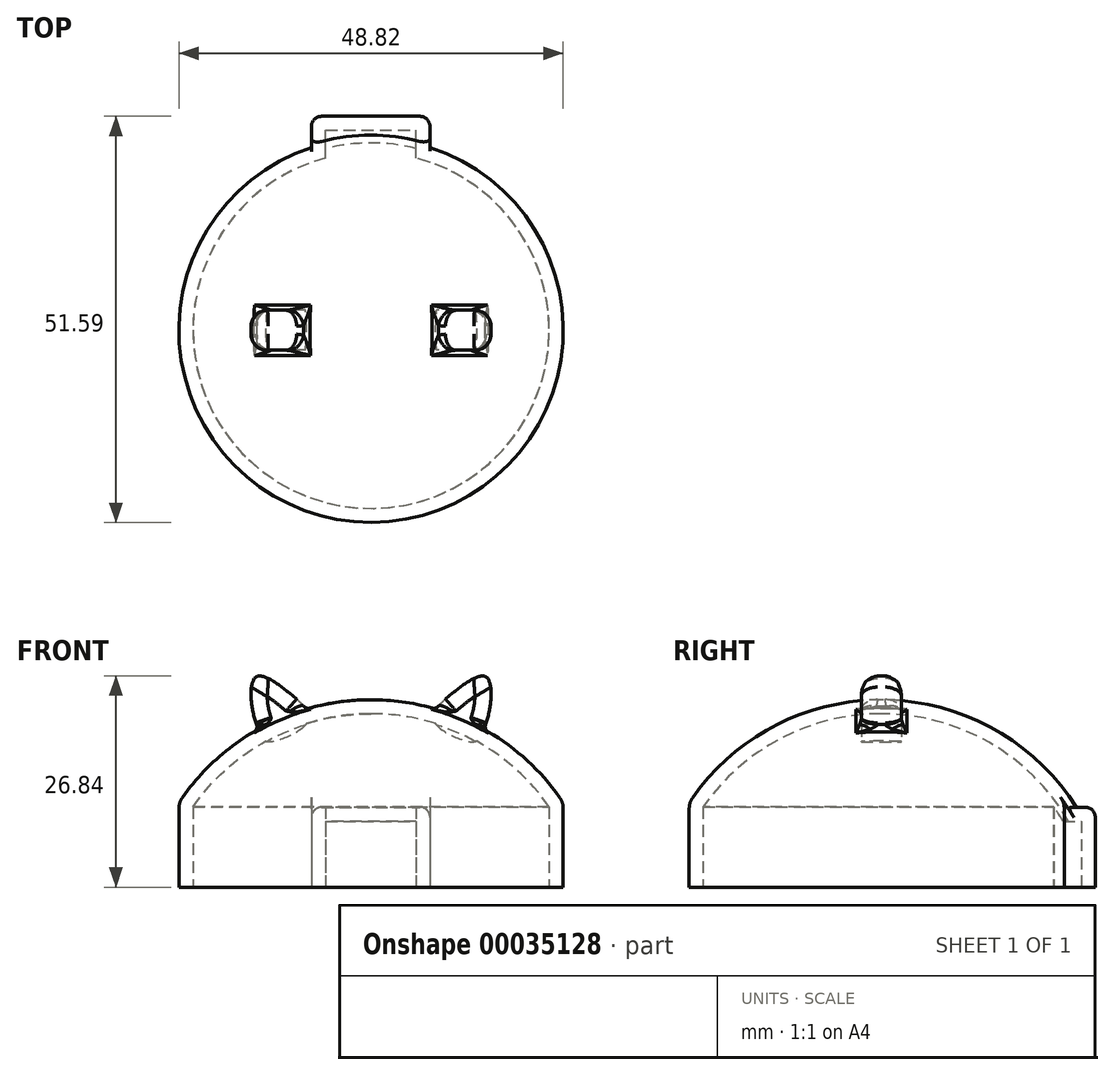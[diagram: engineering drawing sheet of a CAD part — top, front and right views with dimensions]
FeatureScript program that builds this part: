
annotation { "Feature Type Name" : "Feature", "Feature Type Description" : "" }
export const myFeature = defineFeature(function(context is Context, id is Id, definition is map)
    precondition{}
    {
        {
            var Q0;
            Q0=qCreatedBy(makeId("Top.planeOp"),FACE);
            var sketch = newSketch(context, id + "F0", { "sketchPlane" : qUnion([Q0])});
            skCircle(sketch, "E0", {"center": v(0, 0) * mm, "radius": 22.38 * mm});
            skLineSegment(sketch, "E1.bottom", {"start": v(-5.78, 0) * mm, "end": v(5.7, 0) * mm});
            skLineSegment(sketch, "E1.top", {"start": v(-5.78, 25.4) * mm, "end": v(5.7, 25.4) * mm});
            skLineSegment(sketch, "E1.left", {"start": v(-5.78, 0) * mm, "end": v(-5.78, 25.4) * mm});
            skLineSegment(sketch, "E1.right", {"start": v(5.7, 0) * mm, "end": v(5.7, 25.4) * mm});
            skCircle(sketch, "E2.0", {"center": v(0, 0) * mm, "radius": 24.4 * mm});
            skLineSegment(sketch, "E3.0", {"start": v(7.48, 0) * mm, "end": v(7.48, 27.18) * mm});
            skLineSegment(sketch, "E3.1", {"start": v(-7.56, 27.18) * mm, "end": v(7.48, 27.18) * mm});
            skLineSegment(sketch, "E3.2", {"start": v(-7.56, 0) * mm, "end": v(-7.56, 27.18) * mm});
            skLineSegment(sketch, "E4", {"start": v(-7.56, 0) * mm, "end": v(7.48, 0) * mm});
            skSolve(sketch);
        }
        {
            var Q0;
            {var subQ1=sQuery(id+"F0.wireOp",EDGE,"E0");var subQ5=sQuery(id+"F0.wireOp",EDGE,"E3.0");var subQ6=makeQuery(id+"F0.imprint","INTERSECT",VERTEX,{"derivedFrom":[subQ1,subQ5]});Q0=makeQuery(id+"F0.imprint","IMPRINT",FACE,{"disambiguationData":[TD([[makeQuery(id+"F0.imprint","IMPRINT",EDGE,{"disambiguationData":[TD([[subQ6,1.0]])],"derivedFrom":subQ1}),-1.0]])]});}
            var Q1;
            {var subQ1=sQuery(id+"F0.wireOp",EDGE,"E3.0");var subQ7=sQuery(id+"F0.wireOp",EDGE,"E0");var subQ8=makeQuery(id+"F0.imprint","INTERSECT",VERTEX,{"derivedFrom":[subQ7,subQ1]});Q1=makeQuery(id+"F0.imprint","IMPRINT",FACE,{"disambiguationData":[TD([[makeQuery(id+"F0.imprint","IMPRINT",EDGE,{"disambiguationData":[TD([[subQ8,1.0]])],"derivedFrom":subQ7}),1.0]])]});}
            var Q2;
            {var subQ3=sQuery(id+"F0.wireOp",EDGE,"E1.right");var subQ5=sQuery(id+"F0.wireOp",EDGE,"E0");var subQ7=makeQuery(id+"F0.imprint","INTERSECT",VERTEX,{"derivedFrom":[subQ5,subQ3]});Q2=makeQuery(id+"F0.imprint","IMPRINT",FACE,{"disambiguationData":[TD([[makeQuery(id+"F0.imprint","IMPRINT",EDGE,{"disambiguationData":[TD([[subQ7,1.0]])],"derivedFrom":subQ5}),1.0]])]});}
            var Q3;
            {var subQ10=sQuery(id+"F0.wireOp",EDGE,"E1.top");Q3=makeQuery(id+"F0.imprint","IMPRINT",FACE,{"disambiguationData":[TD([[makeQuery(id+"F0.imprint","IMPRINT",EDGE,{"derivedFrom":subQ10}),1.0]])]});}
            var Q4;
            {var subQ5=sQuery(id+"F0.wireOp",EDGE,"E1.top");Q4=makeQuery(id+"F0.imprint","IMPRINT",FACE,{"disambiguationData":[TD([[makeQuery(id+"F0.imprint","IMPRINT",EDGE,{"derivedFrom":subQ5}),-1.0]])]});}
            var Q5;
            {var subQ1=sQuery(id+"F0.wireOp",EDGE,"E1.right");var subQ5=sQuery(id+"F0.wireOp",EDGE,"E0");var subQ6=makeQuery(id+"F0.imprint","INTERSECT",VERTEX,{"derivedFrom":[subQ5,subQ1]});Q5=makeQuery(id+"F0.imprint","IMPRINT",FACE,{"disambiguationData":[TD([[makeQuery(id+"F0.imprint","IMPRINT",EDGE,{"disambiguationData":[TD([[subQ6,-1.0]])],"derivedFrom":subQ5}),-1.0]])]});}
            var Q6;
            {var subQ1=sQuery(id+"F0.wireOp",EDGE,"E1.right");var subQ5=sQuery(id+"F0.wireOp",EDGE,"E0");var subQ7=makeQuery(id+"F0.imprint","INTERSECT",VERTEX,{"derivedFrom":[subQ5,subQ1]});Q6=makeQuery(id+"F0.imprint","IMPRINT",FACE,{"disambiguationData":[TD([[makeQuery(id+"F0.imprint","IMPRINT",EDGE,{"disambiguationData":[TD([[subQ7,1.0]])],"derivedFrom":subQ5}),-1.0]])]});}
            var Q7;
            {var subQ1=sQuery(id+"F0.wireOp",EDGE,"E1.right");var subQ5=sQuery(id+"F0.wireOp",EDGE,"E0");var subQ6=makeQuery(id+"F0.imprint","INTERSECT",VERTEX,{"derivedFrom":[subQ5,subQ1]});Q7=makeQuery(id+"F0.imprint","IMPRINT",FACE,{"disambiguationData":[TD([[makeQuery(id+"F0.imprint","IMPRINT",EDGE,{"disambiguationData":[TD([[subQ6,-1.0]])],"derivedFrom":subQ5}),1.0]])]});}
            var Q8;
            {var subQ3=sQuery(id+"F0.wireOp",EDGE,"E1.left");var subQ5=sQuery(id+"F0.wireOp",EDGE,"E0");var subQ7=makeQuery(id+"F0.imprint","INTERSECT",VERTEX,{"derivedFrom":[subQ5,subQ3]});Q8=makeQuery(id+"F0.imprint","IMPRINT",FACE,{"disambiguationData":[TD([[makeQuery(id+"F0.imprint","IMPRINT",EDGE,{"disambiguationData":[TD([[subQ7,-1.0]])],"derivedFrom":subQ5}),1.0]])]});}
            var Q9;
            {var subQ1=sQuery(id+"F0.wireOp",EDGE,"E0");var subQ5=sQuery(id+"F0.wireOp",EDGE,"E1.left");var subQ7=makeQuery(id+"F0.imprint","INTERSECT",VERTEX,{"derivedFrom":[subQ1,subQ5]});Q9=makeQuery(id+"F0.imprint","IMPRINT",FACE,{"disambiguationData":[TD([[makeQuery(id+"F0.imprint","IMPRINT",EDGE,{"disambiguationData":[TD([[subQ7,-1.0]])],"derivedFrom":subQ1}),-1.0]])]});}
            extrude(context, id + "F1", {"entities" : qUnion([Q0, Q1, Q2, Q3, Q4, Q5, Q6, Q7, Q8, Q9]), "depth" : 25.4 * mm});
        }
        {
            var Q0;
            Q0=qCreatedBy(makeId("Front.planeOp"),FACE);
            var sketch = newSketch(context, id + "F2", { "sketchPlane" : qUnion([Q0])});
            skArc(sketch, "E5", {"start": v(0, 23.8) * mm, "mid": v(-14.15, 20.17) * mm, "end": v(-24.79, 10.16) * mm});
            skLineSegment(sketch, "E6", {"start": v(-24.79, 10.16) * mm, "end": v(-30.56, 10.16) * mm});
            skLineSegment(sketch, "E7", {"start": v(-30.56, 10.16) * mm, "end": v(-30.56, 29.49) * mm});
            skLineSegment(sketch, "E8", {"start": v(-30.56, 29.49) * mm, "end": v(0, 29.49) * mm});
            skLineSegment(sketch, "E9", {"start": v(0, 29.49) * mm, "end": v(0, 23.8) * mm});
            skLineSegment(sketch, "E10", {"start": v(0, -71.32) * mm, "end": v(0, 118.94) * mm, "construction": true});
            skSolve(sketch);
        }
        {
            var Q0;
            Q0 = qSketchRegion(id + "F2", true);
            var Q1;
            Q1=sQuery(id+"F2.wireOp",EDGE,"E10");
            revolve(context, id + "F3", {"operationType" : NewBodyOperationType.REMOVE, "entities" : qUnion([Q0]), "axis" : qUnion([Q1]), "revolveType" : RevolveType.FULL, "oppositeDirection" : true});
        }
        {
            var Q0;
            Q0=qCreatedBy(makeId("Front.planeOp"),FACE);
            var sketch = newSketch(context, id + "F4", { "sketchPlane" : qUnion([Q0])});
            skFitSpline(sketch, "E11", {"points": [v(-14, 19.38) * mm, v(-14.98, 22.19) * mm, v(-14.6, 26.71) * mm, v(-10.27, 24.58) * mm, v(-8.05, 21.05) * mm, v(-13.04, 18.47) * mm, v(-14, 19.38) * mm]});
            skFitSpline(sketch, "E12.MirrorC", {"points": [v(14, 19.38) * mm, v(14.98, 22.19) * mm, v(14.6, 26.71) * mm, v(10.27, 24.58) * mm, v(8.05, 21.05) * mm, v(13.04, 18.47) * mm, v(14, 19.38) * mm]});
            skSolve(sketch);
        }
        {
            var Q0;
            Q0=makeQuery(id+"F1.opExtrude","CAP_FACE",FACE,{"disambiguationData":[OSD([sQuery(id+"F0.wireOp",EDGE,"E2.0"),sQuery(id+"F0.wireOp",EDGE,"E3.0"),sQuery(id+"F0.wireOp",EDGE,"E3.1"),sQuery(id+"F0.wireOp",EDGE,"E3.2")])],"isStart":true});
            shell(context, id + "F5", {"entities" : qUnion([Q0]), "thickness" : 1.78 * mm});
        }
        {
            var Q0;
            Q0=makeQuery(id+"F4.imprint","IMPRINT",FACE,{"disambiguationData":[TD([[makeQuery(id+"F4.imprint","IMPRINT",EDGE,{"derivedFrom":sQuery(id+"F4.wireOp",EDGE,"E11")}),-1.0]])]});
            var Q1;
            Q1=makeQuery(id+"F4.imprint","IMPRINT",FACE,{"disambiguationData":[TD([[makeQuery(id+"F4.imprint","IMPRINT",EDGE,{"derivedFrom":sQuery(id+"F4.wireOp",EDGE,"E12.MirrorC")}),1.0]])]});
            extrude(context, id + "F6", {"entities" : qUnion([Q0, Q1]), "operationType" : NewBodyOperationType.ADD, "endBound" : BoundingType.SYMMETRIC, "depth" : 5.08 * mm});
        }
        {
            var Q0;
            Q0=makeQuery(id+"F6.boolean.opBoolean","INTERSECT",EDGE,{"derivedFrom":[makeQuery(id+"F3.boolean.opBoolean","COPY",FACE,{"derivedFrom":makeQuery(id+"F3.opRevolve","SWEPT_FACE",FACE,{"disambiguationData":[OSD([sQuery(id+"F2.wireOp",EDGE,"E5")])]})}),makeQuery(id+"F6.opExtrude","CAP_FACE",FACE,{"disambiguationData":[OSD([sQuery(id+"F4.wireOp",EDGE,"E11")])],"isStart":false})]});
            var Q1;
            Q1=makeQuery(id+"F6.boolean.opBoolean","INTERSECT",EDGE,{"disambiguationData":[OD(0.0)],"derivedFrom":[makeQuery(id+"F3.boolean.opBoolean","COPY",FACE,{"derivedFrom":makeQuery(id+"F3.opRevolve","SWEPT_FACE",FACE,{"disambiguationData":[OSD([sQuery(id+"F2.wireOp",EDGE,"E5")])]})}),makeQuery(id+"F6.opExtrude","SWEPT_FACE",FACE,{"disambiguationData":[OSD([sQuery(id+"F4.wireOp",EDGE,"E11")])]})]});
            var Q2;
            Q2=makeQuery(id+"F6.boolean.opBoolean","INTERSECT",EDGE,{"derivedFrom":[makeQuery(id+"F3.boolean.opBoolean","COPY",FACE,{"derivedFrom":makeQuery(id+"F3.opRevolve","SWEPT_FACE",FACE,{"disambiguationData":[OSD([sQuery(id+"F2.wireOp",EDGE,"E5")])]})}),makeQuery(id+"F6.opExtrude","CAP_FACE",FACE,{"disambiguationData":[OSD([sQuery(id+"F4.wireOp",EDGE,"E11")])],"isStart":true})]});
            var Q3;
            Q3=makeQuery(id+"F6.boolean.opBoolean","INTERSECT",EDGE,{"disambiguationData":[OD(1.0)],"derivedFrom":[makeQuery(id+"F3.boolean.opBoolean","COPY",FACE,{"derivedFrom":makeQuery(id+"F3.opRevolve","SWEPT_FACE",FACE,{"disambiguationData":[OSD([sQuery(id+"F2.wireOp",EDGE,"E5")])]})}),makeQuery(id+"F6.opExtrude","SWEPT_FACE",FACE,{"disambiguationData":[OSD([sQuery(id+"F4.wireOp",EDGE,"E11")])]})]});
            var Q4;
            Q4=makeQuery(id+"F6.boolean.opBoolean","INTERSECT",EDGE,{"disambiguationData":[OD(0.0)],"derivedFrom":[makeQuery(id+"F3.boolean.opBoolean","COPY",FACE,{"derivedFrom":makeQuery(id+"F3.opRevolve","SWEPT_FACE",FACE,{"disambiguationData":[OSD([sQuery(id+"F2.wireOp",EDGE,"E5")])]})}),makeQuery(id+"F6.opExtrude","SWEPT_FACE",FACE,{"disambiguationData":[OSD([sQuery(id+"F4.wireOp",EDGE,"E12.MirrorC")])]})]});
            var Q5;
            Q5=makeQuery(id+"F6.boolean.opBoolean","INTERSECT",EDGE,{"derivedFrom":[makeQuery(id+"F3.boolean.opBoolean","COPY",FACE,{"derivedFrom":makeQuery(id+"F3.opRevolve","SWEPT_FACE",FACE,{"disambiguationData":[OSD([sQuery(id+"F2.wireOp",EDGE,"E5")])]})}),makeQuery(id+"F6.opExtrude","CAP_FACE",FACE,{"disambiguationData":[OSD([sQuery(id+"F4.wireOp",EDGE,"E12.MirrorC")])],"isStart":false})]});
            var Q6;
            Q6=makeQuery(id+"F6.boolean.opBoolean","INTERSECT",EDGE,{"disambiguationData":[OD(1.0)],"derivedFrom":[makeQuery(id+"F3.boolean.opBoolean","COPY",FACE,{"derivedFrom":makeQuery(id+"F3.opRevolve","SWEPT_FACE",FACE,{"disambiguationData":[OSD([sQuery(id+"F2.wireOp",EDGE,"E5")])]})}),makeQuery(id+"F6.opExtrude","SWEPT_FACE",FACE,{"disambiguationData":[OSD([sQuery(id+"F4.wireOp",EDGE,"E12.MirrorC")])]})]});
            var Q7;
            Q7=makeQuery(id+"F6.boolean.opBoolean","INTERSECT",EDGE,{"derivedFrom":[makeQuery(id+"F3.boolean.opBoolean","COPY",FACE,{"derivedFrom":makeQuery(id+"F3.opRevolve","SWEPT_FACE",FACE,{"disambiguationData":[OSD([sQuery(id+"F2.wireOp",EDGE,"E5")])]})}),makeQuery(id+"F6.opExtrude","CAP_FACE",FACE,{"disambiguationData":[OSD([sQuery(id+"F4.wireOp",EDGE,"E12.MirrorC")])],"isStart":true})]});
            fillet(context, id + "F7", {"entities" : qUnion([Q0, Q1, Q2, Q3, Q4, Q5, Q6, Q7]), "radius" : 0.76 * mm, "tangentPropagation" : true, "allowEdgeOverflow" : false});
        }
        {
            var Q0;
            {var subQ0=sQuery(id+"F4.wireOp",EDGE,"E11");Q0=makeQuery(id+"F6.boolean.opBoolean","SPLIT",EDGE,{"disambiguationData":[TD([makeQuery(id+"F3.boolean.opBoolean","COPY",FACE,{"derivedFrom":makeQuery(id+"F3.opRevolve","SWEPT_FACE",FACE,{"disambiguationData":[OSD([sQuery(id+"F2.wireOp",EDGE,"E5")])]})})])],"derivedFrom":makeQuery(id+"F6.opExtrude","CAP_EDGE",EDGE,{"disambiguationData":[OSD([subQ0])],"isStart":false})});}
            var Q1;
            {var subQ0=sQuery(id+"F4.wireOp",EDGE,"E11");Q1=makeQuery(id+"F6.boolean.opBoolean","SPLIT",EDGE,{"disambiguationData":[TD([makeQuery(id+"F3.boolean.opBoolean","COPY",FACE,{"derivedFrom":makeQuery(id+"F3.opRevolve","SWEPT_FACE",FACE,{"disambiguationData":[OSD([sQuery(id+"F2.wireOp",EDGE,"E5")])]})})])],"derivedFrom":makeQuery(id+"F6.opExtrude","CAP_EDGE",EDGE,{"disambiguationData":[OSD([subQ0])],"isStart":true})});}
            fillet(context, id + "F8", {"entities" : qUnion([Q0, Q1]), "radius" : 2.03 * mm, "tangentPropagation" : true, "allowEdgeOverflow" : false});
        }
        {
            var Q0;
            {var subQ0=sQuery(id+"F4.wireOp",EDGE,"E12.MirrorC");Q0=makeQuery(id+"F6.boolean.opBoolean","SPLIT",EDGE,{"disambiguationData":[TD([makeQuery(id+"F3.boolean.opBoolean","COPY",FACE,{"derivedFrom":makeQuery(id+"F3.opRevolve","SWEPT_FACE",FACE,{"disambiguationData":[OSD([sQuery(id+"F2.wireOp",EDGE,"E5")])]})})])],"derivedFrom":makeQuery(id+"F6.opExtrude","CAP_EDGE",EDGE,{"disambiguationData":[OSD([subQ0])],"isStart":false})});}
            var Q1;
            {var subQ0=sQuery(id+"F4.wireOp",EDGE,"E12.MirrorC");Q1=makeQuery(id+"F6.boolean.opBoolean","SPLIT",EDGE,{"disambiguationData":[TD([makeQuery(id+"F3.boolean.opBoolean","COPY",FACE,{"derivedFrom":makeQuery(id+"F3.opRevolve","SWEPT_FACE",FACE,{"disambiguationData":[OSD([sQuery(id+"F2.wireOp",EDGE,"E5")])]})})])],"derivedFrom":makeQuery(id+"F6.opExtrude","CAP_EDGE",EDGE,{"disambiguationData":[OSD([subQ0])],"isStart":true})});}
            fillet(context, id + "F9", {"entities" : qUnion([Q0, Q1]), "radius" : 2.03 * mm, "tangentPropagation" : true, "allowEdgeOverflow" : false});
        }
        {
            var Q0;
            Q0=makeQuery(id+"F3.boolean.opBoolean","INTERSECT",EDGE,{"derivedFrom":[makeQuery(id+"F1.opExtrude","SWEPT_FACE",FACE,{"disambiguationData":[OSD([sQuery(id+"F0.wireOp",EDGE,"E2.0")])]}),makeQuery(id+"F3.opRevolve","SWEPT_FACE",FACE,{"disambiguationData":[OSD([sQuery(id+"F2.wireOp",EDGE,"E5")])]})]});
            fillet(context, id + "F10", {"entities" : qUnion([Q0]), "radius" : 2.54 * mm, "tangentPropagation" : true, "allowEdgeOverflow" : false});
        }
        {
            var Q0;
            Q0=makeQuery(id+"F3.boolean.opBoolean","INTERSECT",EDGE,{"derivedFrom":[makeQuery(id+"F1.opExtrude","SWEPT_FACE",FACE,{"disambiguationData":[OSD([sQuery(id+"F0.wireOp",EDGE,"E3.1")])]}),makeQuery(id+"F3.opRevolve","SWEPT_FACE",FACE,{"disambiguationData":[OSD([sQuery(id+"F2.wireOp",EDGE,"E6")])]})]});
            var Q1;
            Q1=makeQuery(id+"F1.opExtrude","SWEPT_EDGE",EDGE,{"disambiguationData":[OSD([sQuery(id+"F0.wireOp",EDGE,"E3.0"),sQuery(id+"F0.wireOp",EDGE,"E3.1")])]});
            var Q2;
            Q2=makeQuery(id+"F1.opExtrude","SWEPT_EDGE",EDGE,{"disambiguationData":[OSD([sQuery(id+"F0.wireOp",EDGE,"E3.1"),sQuery(id+"F0.wireOp",EDGE,"E3.2")])]});
            var Q3;
            Q3=makeQuery(id+"F3.boolean.opBoolean","INTERSECT",EDGE,{"derivedFrom":[makeQuery(id+"F1.opExtrude","SWEPT_FACE",FACE,{"disambiguationData":[OSD([sQuery(id+"F0.wireOp",EDGE,"E3.0")])]}),makeQuery(id+"F3.opRevolve","SWEPT_FACE",FACE,{"disambiguationData":[OSD([sQuery(id+"F2.wireOp",EDGE,"E6")])]})]});
            var Q4;
            Q4=makeQuery(id+"F3.boolean.opBoolean","INTERSECT",EDGE,{"derivedFrom":[makeQuery(id+"F1.opExtrude","SWEPT_FACE",FACE,{"disambiguationData":[OSD([sQuery(id+"F0.wireOp",EDGE,"E3.2")])]}),makeQuery(id+"F3.opRevolve","SWEPT_FACE",FACE,{"disambiguationData":[OSD([sQuery(id+"F2.wireOp",EDGE,"E6")])]})]});
            fillet(context, id + "F11", {"entities" : qUnion([Q0, Q1, Q2, Q3, Q4]), "radius" : 1.27 * mm, "tangentPropagation" : true, "allowEdgeOverflow" : false});
        }
    });
